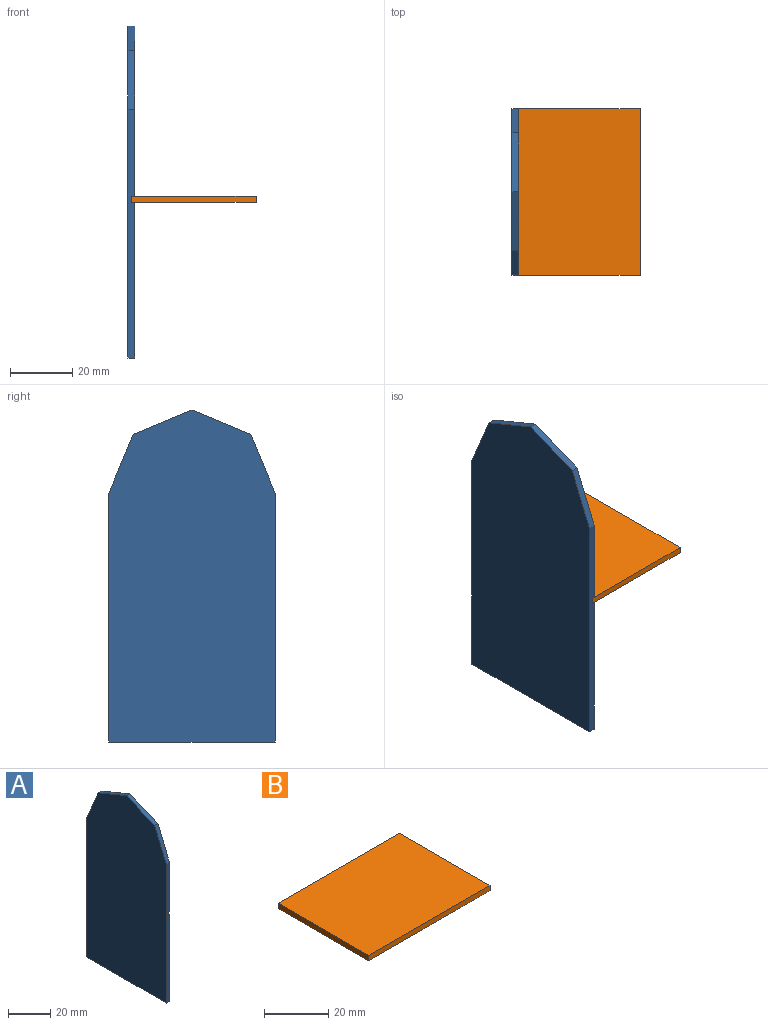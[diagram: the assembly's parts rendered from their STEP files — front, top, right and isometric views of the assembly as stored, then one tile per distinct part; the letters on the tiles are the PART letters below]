
ASSEMBLY  parts=2 mates=1
PART A: 13 faces, bbox 2.2x53.5x106.8 mm
  f0: plane 53.5x50.01mm, normal (1,0,0), area 2675.4mm2, adj f1,f3,f4,f10
  f1: plane 80x2.2mm, normal (0,1,0), area 174mm2, adj f0,f4,f5,f8,f9,f10,f11,f12
  f2: plane 18.92x7.84mm, normal (0,-0.92,0.38), area 45mm2, adj f3,f7,f8,f9
  f3: plane 80x2.2mm, normal (0,-1,0), area 174mm2, adj f0,f2,f4,f8,f9,f10,f11,f12
  f4: plane 53.5x2.2mm, normal (0,0,-1), area 117.7mm2, adj f0,f1,f3,f9
  f5: plane 18.92x7.84mm, normal (0,0.92,0.38), area 45mm2, adj f1,f6,f8,f9
  f6: plane 18.92x7.84mm, normal (0,0.38,0.92), area 45mm2, adj f5,f7,f8,f9
  f7: plane 18.92x7.84mm, normal (0,-0.38,0.92), area 45mm2, adj f2,f6,f8,f9
  f8: plane 54.74x53.5mm, normal (1,0,0), area 2509.6mm2, adj f1,f2,f3,f5,f6,f7,f11
  f9: plane 106.75x53.5mm, normal (-1,0,0), area 5292mm2, adj f1,f2,f3,f4,f5,f6,f7
  f10: plane 53.5x1mm, normal (0,0,1), area 53.5mm2, adj f0,f1,f3,f12
  f11: plane 53.5x1mm, normal (0,0,-1), area 53.5mm2, adj f1,f3,f8,f12
  f12: plane 53.5x2mm, normal (1,0,0), area 107mm2, adj f1,f3,f10,f11
PART B: 6 faces, bbox 53.5x40x2 mm
  f0: plane 53.5x2mm, normal (0,1,0), area 107mm2, adj f1,f3,f4,f5
  f1: plane 40x2mm, normal (-1,0,0), area 80mm2, adj f0,f2,f4,f5
  f2: plane 53.5x2mm, normal (0,-1,0), area 107mm2, adj f1,f3,f4,f5
  f3: plane 40x2mm, normal (1,0,0), area 80mm2, adj f0,f2,f4,f5
  f4: plane 53.5x40mm, normal (0,0,1), area 2140mm2, adj f0,f1,f2,f3
  f5: plane 53.5x40mm, normal (0,0,-1), area 2140mm2, adj f0,f1,f2,f3
PLACE A t=(23.95,21.3,10.22)mm
PLACE B rot(axis=(0,0,-1),90deg) t=(45.15,21.3,20.22)mm
MATE fastened B.f2 <-> A.f12  axis (-1,0,0) through (25.15,-5.45,22.22)mm
